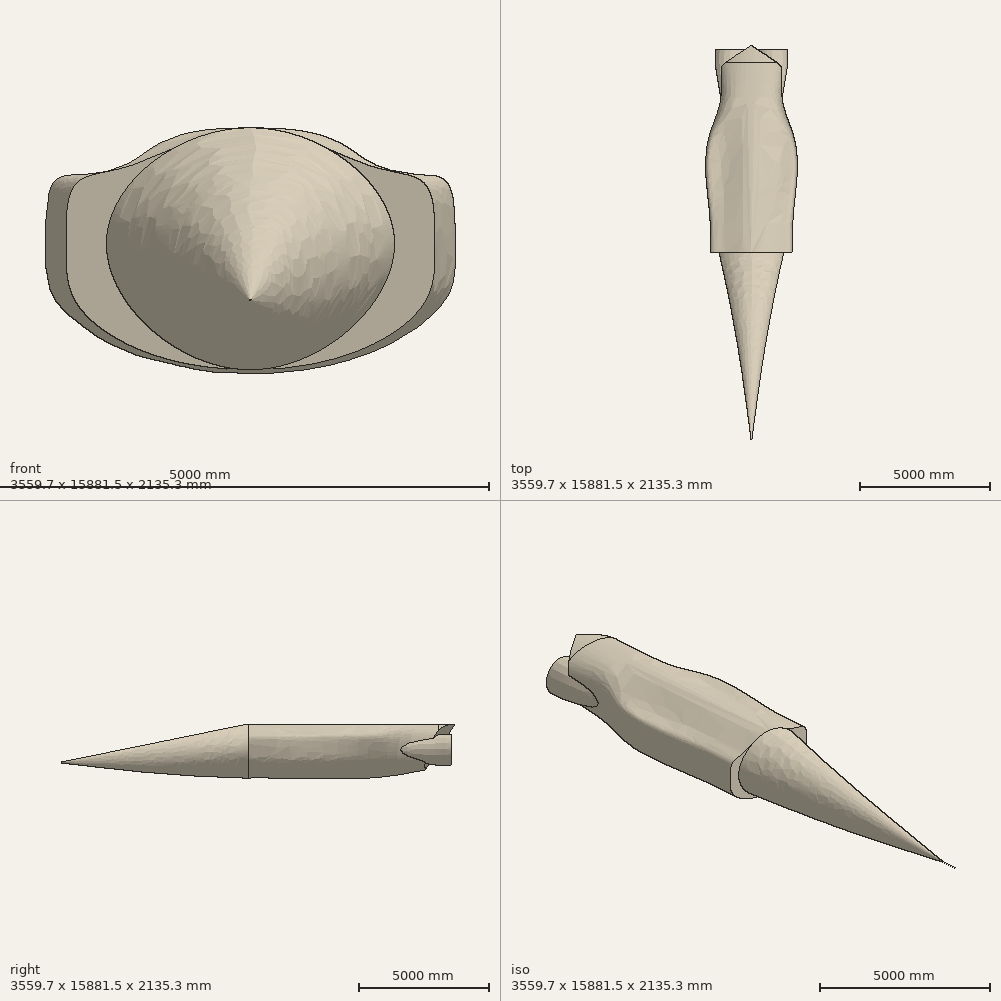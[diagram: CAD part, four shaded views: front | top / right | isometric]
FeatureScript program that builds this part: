
annotation { "Feature Type Name" : "Feature", "Feature Type Description" : "" }
export const myFeature = defineFeature(function(context is Context, id is Id, definition is map)
    precondition{}
    {
        {
            var Q0;
            Q0=qCreatedBy(makeId("Right.planeOp"),FACE);
            var sketch = newSketch(context, id + "F0", { "sketchPlane" : qUnion([Q0])});
            skLineSegment(sketch, "E0", {"start": v(0, 0) * mm, "end": v(-1750, 0) * mm});
            skLineSegment(sketch, "E1", {"start": v(-1750, 0) * mm, "end": v(-3500, 0) * mm});
            skLineSegment(sketch, "E2", {"start": v(-3500, 0) * mm, "end": v(-3500, -1000) * mm});
            skLineSegment(sketch, "E3", {"start": v(-3500, -1000) * mm, "end": v(-8500, -1000) * mm});
            skLineSegment(sketch, "E4", {"start": v(-8500, -1000) * mm, "end": v(-8500, -499.31) * mm});
            skLineSegment(sketch, "E5", {"start": v(-1151.4, 0) * mm, "end": v(-1151.4, 1000) * mm});
            skLineSegment(sketch, "E6", {"start": v(-1151.4, 1000) * mm, "end": v(-8500, -499.31) * mm});
            skLineSegment(sketch, "E7", {"start": v(-8500, -499.31) * mm, "end": v(-3500, -1000) * mm});
            skLineSegment(sketch, "E8", {"start": v(-3500, 0) * mm, "end": v(-3500, 520.82) * mm});
            skLineSegment(sketch, "E9", {"start": v(-8500, -499.31) * mm, "end": v(-8450, -499.31) * mm});
            skLineSegment(sketch, "E10", {"start": v(-8450, -499.31) * mm, "end": v(-8450, -489.1) * mm});
            skLineSegment(sketch, "E11", {"start": v(-8450, -499.31) * mm, "end": v(-8450, -504.32) * mm});
            skSolve(sketch);
        }
        {
            var Q0;
            Q0=sQuery(id+"F0.wireOp",EDGE,"E5");
            cPlane(context, id + "F1", {"entities" : qUnion([Q0]), "cplaneType" : CPlaneType.LINE_ANGLE, "offset" : 25 * mm, "angle" : 90 * degree, "oppositeDirection" : true, "width" : 150 * mm, "height" : 150 * mm});
        }
        {
            var Q0;
            Q0=qCreatedBy(id+"F1.planeOp",FACE);
            var sketch = newSketch(context, id + "F2", { "sketchPlane" : qUnion([Q0])});
            skPoint(sketch, "E12.middle", {"position": v(0, 0) * mm});
            skFitSpline(sketch, "E13", {"points": [v(0, 1000) * mm, v(-1060, 662.5) * mm, v(-1517.6, 506.84) * mm, v(-1600, 0) * mm, v(-1517.6, -506.84) * mm, v(-750, -1000) * mm, v(750, -1000) * mm, v(1517.6, -506.84) * mm, v(1600, 0) * mm, v(1517.6, 506.84) * mm, v(1060, 662.5) * mm, v(0, 1000) * mm]});
            skSolve(sketch);
        }
        {
            var Q0;
            Q0=qCreatedBy(makeId("Front.planeOp"),FACE);
            var sketch = newSketch(context, id + "F3", { "sketchPlane" : qUnion([Q0])});
            skPoint(sketch, "E14.middle", {"position": v(0, 0) * mm});
            skFitSpline(sketch, "E15", {"points": [v(0, 1000) * mm, v(-1060, 662.5) * mm, v(-1517.6, 506.84) * mm, v(-1600, 0) * mm, v(-1517.6, -506.84) * mm, v(-750, -1000) * mm, v(750, -1000) * mm, v(1517.6, -506.84) * mm, v(1600, 0) * mm, v(1517.6, 506.84) * mm, v(1060, 662.5) * mm, v(0, 1000) * mm]});
            skSolve(sketch);
        }
        {
            var Q0;
            Q0=qCreatedBy(makeId("Front.planeOp"),FACE);
            cPlane(context, id + "F4", {"entities" : qUnion([Q0]), "cplaneType" : CPlaneType.OFFSET, "offset" : 3500 * mm, "oppositeDirection" : true, "width" : 150 * mm, "height" : 150 * mm});
        }
        {
            var Q0;
            Q0=qCreatedBy(id+"F4.planeOp",FACE);
            var sketch = newSketch(context, id + "F5", { "sketchPlane" : qUnion([Q0])});
            skPoint(sketch, "E16.middle", {"position": v(0, 0) * mm});
            skFitSpline(sketch, "E17", {"points": [v(0, 1000) * mm, v(-1060, 662.5) * mm, v(-1517.6, 506.84) * mm, v(-1600, 0) * mm, v(-1517.6, -506.84) * mm, v(-750, -1000) * mm, v(750, -1000) * mm, v(1517.6, -506.84) * mm, v(1600, 0) * mm, v(1517.6, 506.84) * mm, v(1060, 662.5) * mm, v(0, 1000) * mm]});
            skSolve(sketch);
        }
        {
            var Q0;
            Q0=qCreatedBy(makeId("Front.planeOp"),FACE);
            cPlane(context, id + "F6", {"entities" : qUnion([Q0]), "cplaneType" : CPlaneType.OFFSET, "offset" : 4500 * mm, "oppositeDirection" : true, "width" : 150 * mm, "height" : 150 * mm});
        }
        {
            var Q0;
            Q0=qCreatedBy(id+"F6.planeOp",FACE);
            var sketch = newSketch(context, id + "F7", { "sketchPlane" : qUnion([Q0])});
            skPoint(sketch, "E18.middle", {"position": v(0, 0) * mm});
            skFitSpline(sketch, "E19", {"points": [v(0, 1000) * mm, v(-1060, 662.5) * mm, v(-1250, 0) * mm, v(-1060, -662.5) * mm, v(0, -1000) * mm, v(1060, -662.5) * mm, v(1250, 0) * mm, v(1060, 662.5) * mm, v(0, 1000) * mm]});
            skSolve(sketch);
        }
        {
            var Q0;
            Q0=qCreatedBy(makeId("Front.planeOp"),FACE);
            cPlane(context, id + "F8", {"entities" : qUnion([Q0]), "cplaneType" : CPlaneType.OFFSET, "offset" : 6232.05 * mm, "oppositeDirection" : true, "width" : 150 * mm, "height" : 150 * mm});
        }
        {
            var Q0;
            Q0=qCreatedBy(id+"F8.planeOp",FACE);
            var sketch = newSketch(context, id + "F9", { "sketchPlane" : qUnion([Q0])});
            skPoint(sketch, "E20.middle", {"position": v(0, 0) * mm});
            skFitSpline(sketch, "E21", {"points": [v(0, 1000) * mm, v(-1060, 662.5) * mm, v(-1250, 0) * mm, v(-848, -530) * mm, v(848, -530) * mm, v(1250, 0) * mm, v(1060, 662.5) * mm, v(0, 1000) * mm]});
            skSolve(sketch);
        }
        {
            var Q0;
            Q0=makeQuery(id+"F2.imprint","IMPRINT",FACE,{"disambiguationData":[TD([[makeQuery(id+"F2.imprint","IMPRINT",EDGE,{"derivedFrom":sQuery(id+"F2.wireOp",EDGE,"E13")}),1.0]])]});
            var Q1;
            Q1=makeQuery(id+"F3.imprint","IMPRINT",FACE,{"disambiguationData":[TD([[makeQuery(id+"F3.imprint","IMPRINT",EDGE,{"derivedFrom":sQuery(id+"F3.wireOp",EDGE,"E15")}),1.0]])]});
            var Q2;
            Q2=makeQuery(id+"F5.imprint","IMPRINT",FACE,{"disambiguationData":[TD([[makeQuery(id+"F5.imprint","IMPRINT",EDGE,{"derivedFrom":sQuery(id+"F5.wireOp",EDGE,"E17")}),1.0]])]});
            var Q3;
            Q3=makeQuery(id+"F7.imprint","IMPRINT",FACE,{"disambiguationData":[TD([[makeQuery(id+"F7.imprint","IMPRINT",EDGE,{"derivedFrom":sQuery(id+"F7.wireOp",EDGE,"E19")}),1.0]])]});
            var Q4;
            Q4=makeQuery(id+"F9.imprint","IMPRINT",FACE,{"disambiguationData":[TD([[makeQuery(id+"F9.imprint","IMPRINT",EDGE,{"derivedFrom":sQuery(id+"F9.wireOp",EDGE,"E21")}),1.0]])]});
            loft(context, id + "F10", {"sheetProfilesArray" : [{ "sheetProfileEntities" : qUnion([Q0]) }, { "sheetProfileEntities" : qUnion([Q1]) }, { "sheetProfileEntities" : qUnion([Q2]) }, { "sheetProfileEntities" : qUnion([Q3]) }, { "sheetProfileEntities" : qUnion([Q4]) }]});
        }
        {
            var Q0;
            Q0=makeQuery(id+"F10.opLoft","CAP_FACE",FACE,{"disambiguationData":[OSD([makeQuery(id+"F9.imprint","IMPRINT",FACE,{"disambiguationData":[TD([[makeQuery(id+"F9.imprint","IMPRINT",EDGE,{"derivedFrom":sQuery(id+"F9.wireOp",EDGE,"E21")}),1.0]])]})])],"isStart":true});
            extrude(context, id + "F11", {"entities" : qUnion([Q0]), "operationType" : NewBodyOperationType.ADD, "depth" : 649.4 * mm, "offsetDistance" : 25 * mm});
        }
        {
            var Q0;
            Q0=qCreatedBy(makeId("Right.planeOp"),FACE);
            var sketch = newSketch(context, id + "F12", { "sketchPlane" : qUnion([Q0])});
            skLineSegment(sketch, "E22", {"start": v(0, 0) * mm, "end": v(4500, 0) * mm});
            skLineSegment(sketch, "E23", {"start": v(4500, 0) * mm, "end": v(6232.05, 0) * mm});
            skLineSegment(sketch, "E24", {"start": v(4500, 0) * mm, "end": v(4500, 1000) * mm});
            skLineSegment(sketch, "E25", {"start": v(4500, 1000) * mm, "end": v(6881.46, 1000) * mm});
            skLineSegment(sketch, "E26", {"start": v(6881.46, 1000) * mm, "end": v(6881.46, -1000) * mm});
            skLineSegment(sketch, "E27", {"start": v(6881.46, 1000) * mm, "end": v(6232.05, 0) * mm});
            skLineSegment(sketch, "E28", {"start": v(6232.05, 0) * mm, "end": v(5582.64, -1000) * mm});
            skLineSegment(sketch, "E29", {"start": v(5582.64, -1000) * mm, "end": v(6881.46, -1000) * mm});
            skSolve(sketch);
        }
        {
            var Q0;
            Q0=makeQuery(id+"F12.imprint","IMPRINT",FACE,{"disambiguationData":[TD([[makeQuery(id+"F12.imprint","IMPRINT",EDGE,{"derivedFrom":sQuery(id+"F12.wireOp",EDGE,"E26")}),-1.0]])]});
            var Q1;
            Q1=sQuery(id+"F12.wireOp",EDGE,"E25");
            revolve(context, id + "F13", {"operationType" : NewBodyOperationType.REMOVE, "entities" : qUnion([Q0]), "axis" : qUnion([Q1]), "revolveType" : RevolveType.SYMMETRIC, "oppositeDirection" : true, "angle" : 182 * degree});
        }
        {
            var Q0;
            Q0=qCreatedBy(id+"F1.planeOp",FACE);
            var sketch = newSketch(context, id + "F14", { "sketchPlane" : qUnion([Q0])});
            skFitSpline(sketch, "E30", {"points": [v(0, 1000) * mm, v(-1250, 0) * mm, v(0, -1099.92) * mm, v(1250, 0) * mm, v(0, 1000) * mm]});
            skSolve(sketch);
        }
        {
            var Q0;
            Q0=qCreatedBy(makeId("Front.planeOp"),FACE);
            cPlane(context, id + "F15", {"entities" : qUnion([Q0]), "cplaneType" : CPlaneType.OFFSET, "offset" : 3500 * mm, "width" : 150 * mm, "height" : 150 * mm});
        }
        {
            var Q0;
            Q0=qCreatedBy(id+"F15.planeOp",FACE);
            var sketch = newSketch(context, id + "F16", { "sketchPlane" : qUnion([Q0])});
            skCircle(sketch, "E31", {"center": v(0, -239.59) * mm, "radius": 760.41 * mm});
            skSolve(sketch);
        }
        {
            var Q0;
            Q0=qCreatedBy(makeId("Front.planeOp"),FACE);
            cPlane(context, id + "F17", {"entities" : qUnion([Q0]), "cplaneType" : CPlaneType.OFFSET, "offset" : 8450 * mm, "width" : 150 * mm, "height" : 150 * mm});
        }
        {
            var Q0;
            Q0=qCreatedBy(id+"F17.planeOp",FACE);
            var sketch = newSketch(context, id + "F18", { "sketchPlane" : qUnion([Q0])});
            skCircle(sketch, "E32", {"center": v(0, -496.71) * mm, "radius": 7.6 * mm});
            skSolve(sketch);
        }
        {
            var Q1;
            Q1=makeQuery(id+"F18.imprint","IMPRINT",FACE,{"disambiguationData":[TD([[makeQuery(id+"F18.imprint","IMPRINT",EDGE,{"derivedFrom":sQuery(id+"F18.wireOp",EDGE,"E32")}),1.0]])]});
            var Q2;
            Q2=makeQuery(id+"F16.imprint","IMPRINT",FACE,{"disambiguationData":[TD([[makeQuery(id+"F16.imprint","IMPRINT",EDGE,{"derivedFrom":sQuery(id+"F16.wireOp",EDGE,"E31")}),1.0]])]});
            var Q3;
            Q3=makeQuery(id+"F14.imprint","IMPRINT",FACE,{"disambiguationData":[TD([[makeQuery(id+"F14.imprint","IMPRINT",EDGE,{"derivedFrom":sQuery(id+"F14.wireOp",EDGE,"E30")}),1.0]])]});
            loft(context, id + "F19", {"operationType" : NewBodyOperationType.ADD, "sheetProfilesArray" : [{ "sheetProfileEntities" : qUnion([Q1]) }, { "sheetProfileEntities" : qUnion([Q2]) }, { "sheetProfileEntities" : qUnion([Q3]) }]});
        }
        {
            var Q0;
            Q0=makeQuery(id+"F19.opLoft","CAP_FACE",FACE,{"disambiguationData":[OSD([makeQuery(id+"F18.imprint","IMPRINT",FACE,{"disambiguationData":[TD([[makeQuery(id+"F18.imprint","IMPRINT",EDGE,{"derivedFrom":sQuery(id+"F18.wireOp",EDGE,"E32")}),1.0]])]})])],"isStart":true});
            extrude(context, id + "F20", {"entities" : qUnion([Q0]), "operationType" : NewBodyOperationType.ADD, "depth" : 550 * mm, "offsetDistance" : 25 * mm});
        }
        {
            var Q0;
            Q0=qCreatedBy(makeId("Front.planeOp"),FACE);
            cPlane(context, id + "F21", {"entities" : qUnion([Q0]), "cplaneType" : CPlaneType.OFFSET, "offset" : 3500 * mm, "oppositeDirection" : true, "width" : 150 * mm, "height" : 150 * mm});
        }
        {
            var Q0;
            Q0=qCreatedBy(id+"F21.planeOp",FACE);
            var sketch = newSketch(context, id + "F22", { "sketchPlane" : qUnion([Q0])});
            skCircle(sketch, "E33", {"center": v(-800, 0) * mm, "radius": 600 * mm});
            skCircle(sketch, "E34", {"center": v(800, 0) * mm, "radius": 600 * mm});
            skSolve(sketch);
        }
        {
            var Q0;
            Q0=qCreatedBy(makeId("Front.planeOp"),FACE);
            cPlane(context, id + "F23", {"entities" : qUnion([Q0]), "cplaneType" : CPlaneType.OFFSET, "offset" : 4500 * mm, "oppositeDirection" : true, "width" : 150 * mm, "height" : 150 * mm});
        }
        {
            var Q0;
            Q0=qCreatedBy(id+"F23.planeOp",FACE);
            var sketch = newSketch(context, id + "F24", { "sketchPlane" : qUnion([Q0])});
            skCircle(sketch, "E35", {"center": v(-800, 0) * mm, "radius": 400 * mm});
            skCircle(sketch, "E36", {"center": v(800, 0) * mm, "radius": 400 * mm});
            skSolve(sketch);
        }
        {
            var Q0;
            Q0=qCreatedBy(makeId("Front.planeOp"),FACE);
            cPlane(context, id + "F25", {"entities" : qUnion([Q0]), "cplaneType" : CPlaneType.OFFSET, "offset" : 6232.05 * mm, "oppositeDirection" : true, "width" : 150 * mm, "height" : 150 * mm});
        }
        {
            var Q0;
            Q0=qCreatedBy(id+"F25.planeOp",FACE);
            var sketch = newSketch(context, id + "F26", { "sketchPlane" : qUnion([Q0])});
            skCircle(sketch, "E37", {"center": v(-800, 0) * mm, "radius": 600 * mm});
            skCircle(sketch, "E38", {"center": v(800, 0) * mm, "radius": 600 * mm});
            skSolve(sketch);
        }
        {
            var Q0;
            Q0=qCreatedBy(makeId("Front.planeOp"),FACE);
            cPlane(context, id + "F27", {"entities" : qUnion([Q0]), "cplaneType" : CPlaneType.OFFSET, "offset" : 6732.05 * mm, "oppositeDirection" : true, "width" : 150 * mm, "height" : 150 * mm});
        }
        {
            var Q0;
            Q0=qCreatedBy(id+"F27.planeOp",FACE);
            var sketch = newSketch(context, id + "F28", { "sketchPlane" : qUnion([Q0])});
            skCircle(sketch, "E39", {"center": v(-800, 0) * mm, "radius": 600 * mm});
            skCircle(sketch, "E40", {"center": v(800, 0) * mm, "radius": 600 * mm});
            skSolve(sketch);
        }
        {
            var Q0;
            Q0=makeQuery(id+"F22.imprint","IMPRINT",FACE,{"disambiguationData":[TD([[makeQuery(id+"F22.imprint","IMPRINT",EDGE,{"derivedFrom":sQuery(id+"F22.wireOp",EDGE,"E33")}),1.0]])]});
            var Q1;
            Q1=makeQuery(id+"F24.imprint","IMPRINT",FACE,{"disambiguationData":[TD([[makeQuery(id+"F24.imprint","IMPRINT",EDGE,{"derivedFrom":sQuery(id+"F24.wireOp",EDGE,"E35")}),1.0]])]});
            var Q2;
            Q2=makeQuery(id+"F26.imprint","IMPRINT",FACE,{"disambiguationData":[TD([[makeQuery(id+"F26.imprint","IMPRINT",EDGE,{"derivedFrom":sQuery(id+"F26.wireOp",EDGE,"E37")}),1.0]])]});
            var Q3;
            Q3=makeQuery(id+"F28.imprint","IMPRINT",FACE,{"disambiguationData":[TD([[makeQuery(id+"F28.imprint","IMPRINT",EDGE,{"derivedFrom":sQuery(id+"F28.wireOp",EDGE,"E39")}),1.0]])]});
            loft(context, id + "F29", {"sheetProfilesArray" : [{ "sheetProfileEntities" : qUnion([Q0]) }, { "sheetProfileEntities" : qUnion([Q1]) }, { "sheetProfileEntities" : qUnion([Q2]) }, { "sheetProfileEntities" : qUnion([Q3]) }]});
        }
        {
            var Q0;
            Q0=makeQuery(id+"F22.imprint","IMPRINT",FACE,{"disambiguationData":[TD([[makeQuery(id+"F22.imprint","IMPRINT",EDGE,{"derivedFrom":sQuery(id+"F22.wireOp",EDGE,"E34")}),1.0]])]});
            var Q1;
            Q1=makeQuery(id+"F24.imprint","IMPRINT",FACE,{"disambiguationData":[TD([[makeQuery(id+"F24.imprint","IMPRINT",EDGE,{"derivedFrom":sQuery(id+"F24.wireOp",EDGE,"E36")}),1.0]])]});
            var Q2;
            Q2=makeQuery(id+"F26.imprint","IMPRINT",FACE,{"disambiguationData":[TD([[makeQuery(id+"F26.imprint","IMPRINT",EDGE,{"derivedFrom":sQuery(id+"F26.wireOp",EDGE,"E38")}),1.0]])]});
            var Q3;
            Q3=makeQuery(id+"F28.imprint","IMPRINT",FACE,{"disambiguationData":[TD([[makeQuery(id+"F28.imprint","IMPRINT",EDGE,{"derivedFrom":sQuery(id+"F28.wireOp",EDGE,"E40")}),1.0]])]});
            loft(context, id + "F30", {"sheetProfilesArray" : [{ "sheetProfileEntities" : qUnion([Q0]) }, { "sheetProfileEntities" : qUnion([Q1]) }, { "sheetProfileEntities" : qUnion([Q2]) }, { "sheetProfileEntities" : qUnion([Q3]) }]});
        }
    });
